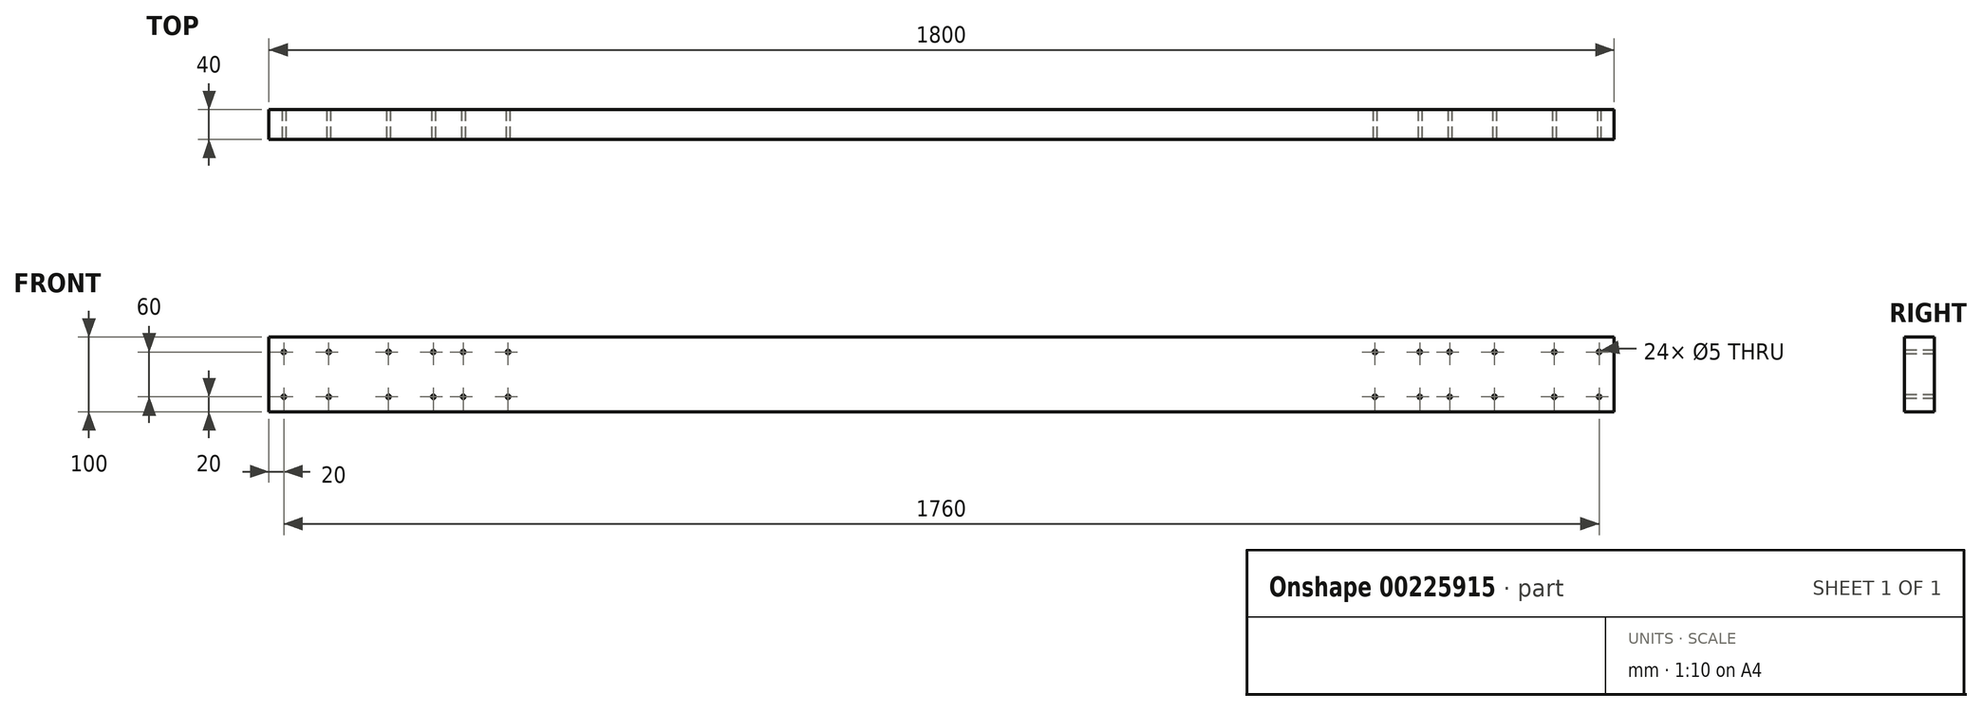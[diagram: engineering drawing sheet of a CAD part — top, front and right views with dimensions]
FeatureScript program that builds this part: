
annotation { "Feature Type Name" : "Feature", "Feature Type Description" : "" }
export const myFeature = defineFeature(function(context is Context, id is Id, definition is map)
    precondition{}
    {
        {
            var Q0;
            Q0=qCreatedBy(makeId("Front.planeOp"),FACE);
            var sketch = newSketch(context, id + "F0", { "sketchPlane" : qUnion([Q0])});
            skLineSegment(sketch, "E0.bottom", {"start": v(-900, 50) * mm, "end": v(900, 50) * mm});
            skLineSegment(sketch, "E0.top", {"start": v(-900, -50) * mm, "end": v(900, -50) * mm});
            skLineSegment(sketch, "E0.left", {"start": v(-900, 50) * mm, "end": v(-900, -50) * mm});
            skLineSegment(sketch, "E0.right", {"start": v(900, 50) * mm, "end": v(900, -50) * mm});
            skLineSegment(sketch, "E1", {"start": v(0, 50) * mm, "end": v(0, -50) * mm, "construction": true});
            skLineSegment(sketch, "E2", {"start": v(-900, 0) * mm, "end": v(900, 0) * mm, "construction": true});
            skSolve(sketch);
        }
        {
            var Q0;
            Q0=makeQuery(id+"F0.imprint","IMPRINT",FACE,{"disambiguationData":[TD([[makeQuery(id+"F0.imprint","IMPRINT",EDGE,{"derivedFrom":sQuery(id+"F0.wireOp",EDGE,"E0.bottom")}),-1.0]])]});
            extrude(context, id + "F1", {"entities" : qUnion([Q0]), "endBound" : BoundingType.SYMMETRIC, "depth" : 40 * mm});
        }
        {
            var Q0;
            Q0=makeQuery(id+"F1.opExtrude","CAP_FACE",FACE,{"disambiguationData":[OSD([sQuery(id+"F0.wireOp",EDGE,"E0.bottom"),sQuery(id+"F0.wireOp",EDGE,"E0.top"),sQuery(id+"F0.wireOp",EDGE,"E0.left"),sQuery(id+"F0.wireOp",EDGE,"E0.right")])],"isStart":false});
            var sketch = newSketch(context, id + "F2", { "sketchPlane" : qUnion([Q0])});
            skPoint(sketch, "E3", {"position": v(-880, 30) * mm});
            skPoint(sketch, "E4", {"position": v(-820, 30) * mm});
            skPoint(sketch, "E5", {"position": v(-880, -30) * mm});
            skPoint(sketch, "E6", {"position": v(-820, -30) * mm});
            skPoint(sketch, "E7", {"position": v(880, 30) * mm});
            skPoint(sketch, "E8", {"position": v(880, -30) * mm});
            skPoint(sketch, "E9", {"position": v(820, 30) * mm});
            skPoint(sketch, "E10", {"position": v(820, -30) * mm});
            skPoint(sketch, "E11", {"position": v(-740, 30) * mm});
            skPoint(sketch, "E12", {"position": v(-680, 30) * mm});
            skPoint(sketch, "E13", {"position": v(-740, -30) * mm});
            skPoint(sketch, "E14", {"position": v(-680, -30) * mm});
            skPoint(sketch, "E15", {"position": v(740, 30) * mm});
            skPoint(sketch, "E16", {"position": v(680, 30) * mm});
            skPoint(sketch, "E17", {"position": v(680, -30) * mm});
            skPoint(sketch, "E18", {"position": v(740, -30) * mm});
            skPoint(sketch, "E19", {"position": v(-640, 30) * mm});
            skPoint(sketch, "E20", {"position": v(-580, 30) * mm});
            skPoint(sketch, "E21", {"position": v(-640, -30) * mm});
            skPoint(sketch, "E22", {"position": v(-580, -30) * mm});
            skPoint(sketch, "E23", {"position": v(640, 30) * mm});
            skPoint(sketch, "E24", {"position": v(580, 30) * mm});
            skPoint(sketch, "E25", {"position": v(580, -30) * mm});
            skPoint(sketch, "E26", {"position": v(640, -30) * mm});
            skSolve(sketch);
        }
        {
            var Q0;
            Q0=sQuery(id+"F2.wireOp",VERTEX,"E3");
            var Q1;
            Q1=sQuery(id+"F2.wireOp",VERTEX,"E5");
            var Q2;
            Q2=sQuery(id+"F2.wireOp",VERTEX,"E4");
            var Q3;
            Q3=sQuery(id+"F2.wireOp",VERTEX,"E6");
            var Q4;
            Q4=sQuery(id+"F2.wireOp",VERTEX,"E11");
            var Q5;
            Q5=sQuery(id+"F2.wireOp",VERTEX,"E13");
            var Q6;
            Q6=sQuery(id+"F2.wireOp",VERTEX,"E12");
            var Q7;
            Q7=sQuery(id+"F2.wireOp",VERTEX,"E14");
            var Q8;
            Q8=sQuery(id+"F2.wireOp",VERTEX,"E16");
            var Q9;
            Q9=sQuery(id+"F2.wireOp",VERTEX,"E17");
            var Q10;
            Q10=sQuery(id+"F2.wireOp",VERTEX,"E15");
            var Q11;
            Q11=sQuery(id+"F2.wireOp",VERTEX,"E18");
            var Q12;
            Q12=sQuery(id+"F2.wireOp",VERTEX,"E10");
            var Q13;
            Q13=sQuery(id+"F2.wireOp",VERTEX,"E7");
            var Q14;
            Q14=sQuery(id+"F2.wireOp",VERTEX,"E8");
            var Q15;
            Q15=sQuery(id+"F2.wireOp",VERTEX,"E9");
            var Q16;
            Q16=sQuery(id+"F2.wireOp",VERTEX,"E19");
            var Q17;
            Q17=sQuery(id+"F2.wireOp",VERTEX,"E21");
            var Q18;
            Q18=sQuery(id+"F2.wireOp",VERTEX,"E22");
            var Q19;
            Q19=sQuery(id+"F2.wireOp",VERTEX,"E20");
            var Q20;
            Q20=sQuery(id+"F2.wireOp",VERTEX,"E24");
            var Q21;
            Q21=sQuery(id+"F2.wireOp",VERTEX,"E23");
            var Q22;
            Q22=sQuery(id+"F2.wireOp",VERTEX,"E25");
            var Q23;
            Q23=sQuery(id+"F2.wireOp",VERTEX,"E26");
            var Q24;
            Q24=makeQuery(id+"F1.opExtrude","SWEPT_BODY",BODY,{"disambiguationData":[OSD([sQuery(id+"F0.wireOp",EDGE,"E0.bottom"),sQuery(id+"F0.wireOp",EDGE,"E0.top"),sQuery(id+"F0.wireOp",EDGE,"E0.left"),sQuery(id+"F0.wireOp",EDGE,"E0.right")])]});
            hole(context, id + "F3", {"style" : HoleStyle.SIMPLE, "endStyle" : HoleEndStyle.THROUGH, "holeDiameter" : 5 * mm, "locations" : qUnion([Q0, Q1, Q2, Q3, Q4, Q5, Q6, Q7, Q8, Q9, Q10, Q11, Q12, Q13, Q14, Q15, Q16, Q17, Q18, Q19, Q20, Q21, Q22, Q23]), "scope" : qUnion([Q24]), "isTappedThrough" : true});
        }
    });
